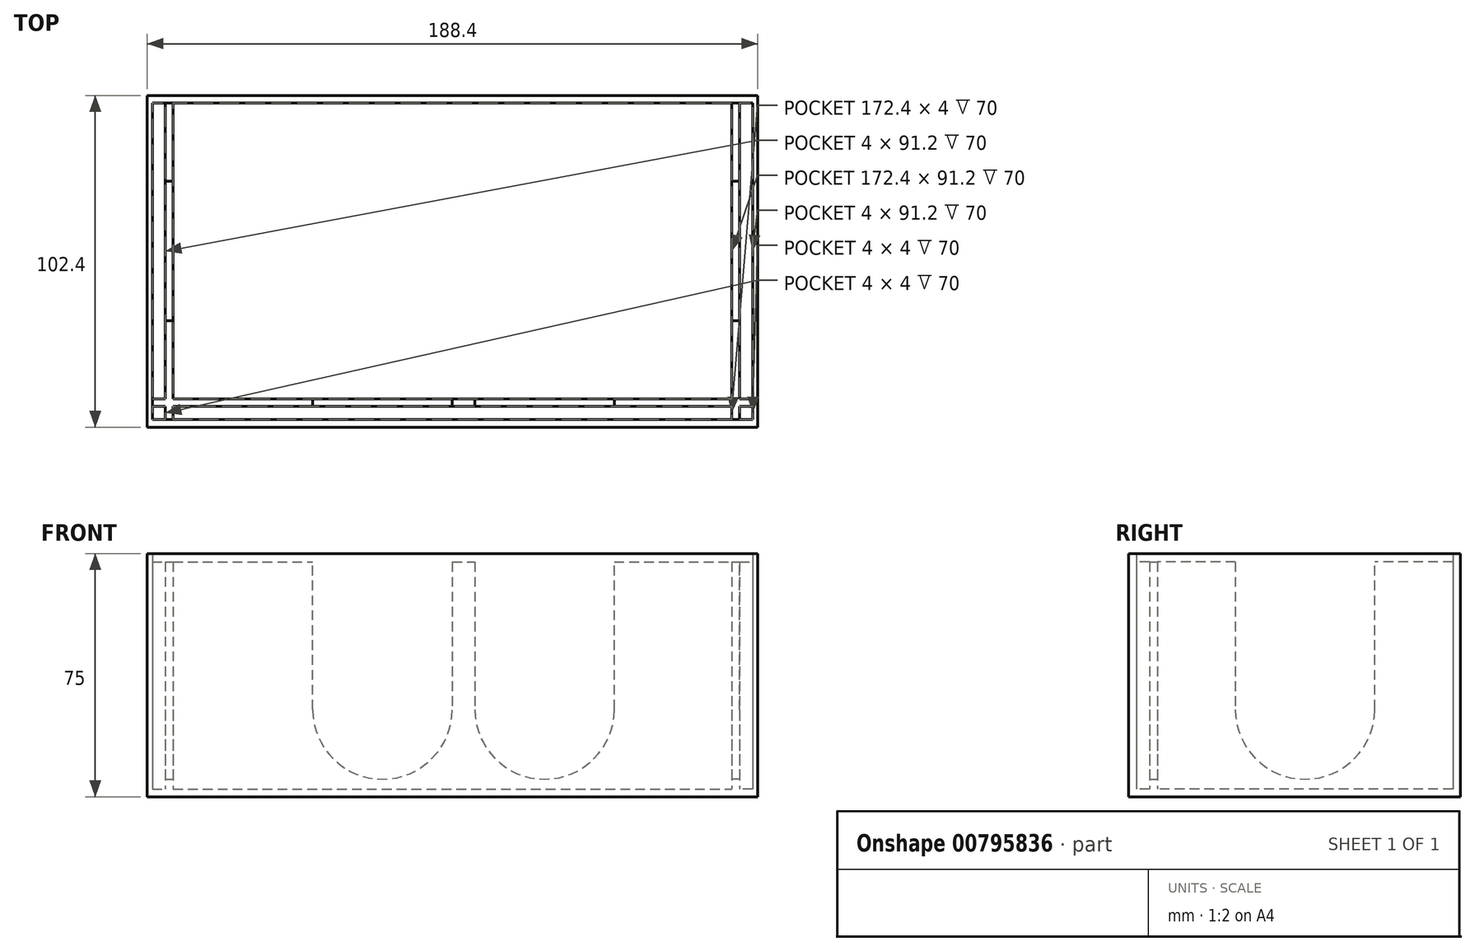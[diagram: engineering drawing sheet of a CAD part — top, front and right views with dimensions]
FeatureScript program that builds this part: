
annotation { "Feature Type Name" : "Feature", "Feature Type Description" : "" }
export const myFeature = defineFeature(function(context is Context, id is Id, definition is map)
    precondition{}
    {
        {
            var Q0;
            Q0=qCreatedBy(makeId("Top.planeOp"),FACE);
            var sketch = newSketch(context, id + "F0", { "sketchPlane" : qUnion([Q0]) });
            skLineSegment(sketch, "E0", {"start": v(-98.41, -24.68) * mm, "end": v(91.59, -24.68) * mm});
            skLineSegment(sketch, "E1", {"start": v(91.59, -24.68) * mm, "end": v(91.59, 77.72) * mm});
            skLineSegment(sketch, "E2", {"start": v(91.59, 77.72) * mm, "end": v(-98.41, 77.72) * mm});
            skLineSegment(sketch, "E3", {"start": v(-98.41, 77.72) * mm, "end": v(-98.41, -24.68) * mm});
            skSolve(sketch);
        }
        {
            var Q0;
            Q0 = qSketchRegion(id + "F0", true);
            extrude(context, id + "F1", {"entities" : qUnion([Q0]), "depth" : 75 * mm, "offsetDistance" : 25 * mm});
        }
        {
            var Q0;
            Q0=makeQuery(id+"F1.opExtrude","CAP_FACE",FACE,{"disambiguationData":[OSD([sQuery(id+"F0.wireOp",EDGE,"E0"),sQuery(id+"F0.wireOp",EDGE,"E1"),sQuery(id+"F0.wireOp",EDGE,"E2"),sQuery(id+"F0.wireOp",EDGE,"E3")])],"isStart":false});
            shell(context, id + "F2", {"entities" : qUnion([Q0]), "thickness" : 2.4 * mm});
        }
        {
            var Q0;
            Q0=makeQuery(id+"F2.opShell","OFFSET_FACE",FACE,{"disambiguationData":[OSD([sQuery(id+"F0.wireOp",EDGE,"E0"),sQuery(id+"F0.wireOp",EDGE,"E1"),sQuery(id+"F0.wireOp",EDGE,"E2"),sQuery(id+"F0.wireOp",EDGE,"E3")])]});
            var sketch = newSketch(context, id + "F3", { "sketchPlane" : qUnion([Q0]) });
            skLineSegment(sketch, "E4", {"start": v(-96.01, 75.32) * mm, "end": v(-92.01, 75.32) * mm, "construction": true});
            skLineSegment(sketch, "E5", {"start": v(-92.01, 75.32) * mm, "end": v(-89.61, 75.32) * mm});
            skLineSegment(sketch, "E6", {"start": v(-96.01, -22.28) * mm, "end": v(-96.01, -18.28) * mm, "construction": true});
            skLineSegment(sketch, "E7", {"start": v(-96.01, -18.28) * mm, "end": v(-96.01, -15.88) * mm});
            skLineSegment(sketch, "E8", {"start": v(89.19, 75.32) * mm, "end": v(85.19, 75.32) * mm, "construction": true});
            skLineSegment(sketch, "E9", {"start": v(85.19, 75.32) * mm, "end": v(82.79, 75.32) * mm});
            skLineSegment(sketch, "E10", {"start": v(-92.01, 75.32) * mm, "end": v(-92.01, -15.88) * mm});
            skLineSegment(sketch, "E11", {"start": v(-89.61, 75.32) * mm, "end": v(-89.61, -15.88) * mm});
            skLineSegment(sketch, "E12", {"start": v(-96.01, -18.28) * mm, "end": v(-92.01, -18.28) * mm});
            skLineSegment(sketch, "E13", {"start": v(-96.01, -15.88) * mm, "end": v(-92.01, -15.88) * mm});
            skLineSegment(sketch, "E14", {"start": v(85.19, 75.32) * mm, "end": v(85.19, -15.88) * mm});
            skLineSegment(sketch, "E15", {"start": v(82.79, 75.32) * mm, "end": v(82.79, -15.88) * mm});
            skLineSegment(sketch, "E16.trimOffspring", {"start": v(85.19, -15.88) * mm, "end": v(89.19, -15.88) * mm});
            skLineSegment(sketch, "E17.trimOffspring", {"start": v(82.79, -18.28) * mm, "end": v(82.79, -22.28) * mm});
            skLineSegment(sketch, "E18.trimOffspring", {"start": v(85.19, -18.28) * mm, "end": v(85.19, -22.28) * mm});
            skLineSegment(sketch, "E19.trimOffspring", {"start": v(85.19, -18.28) * mm, "end": v(89.19, -18.28) * mm});
            skLineSegment(sketch, "E20.trimOffspring", {"start": v(-89.61, -18.28) * mm, "end": v(82.79, -18.28) * mm});
            skLineSegment(sketch, "E21.trimOffspring", {"start": v(-89.61, -15.88) * mm, "end": v(82.79, -15.88) * mm});
            skLineSegment(sketch, "E22.trimOffspring", {"start": v(-92.01, -18.28) * mm, "end": v(-92.01, -22.28) * mm});
            skLineSegment(sketch, "E23.trimOffspring", {"start": v(-89.61, -18.28) * mm, "end": v(-89.61, -22.28) * mm});
            skLineSegment(sketch, "E24", {"start": v(-92.01, -22.28) * mm, "end": v(-89.61, -22.28) * mm});
            skLineSegment(sketch, "E25", {"start": v(82.79, -22.28) * mm, "end": v(85.19, -22.28) * mm});
            skLineSegment(sketch, "E26", {"start": v(89.19, -15.88) * mm, "end": v(89.19, -18.28) * mm});
            skLineSegment(sketch, "E27", {"start": v(82.79, 75.32) * mm, "end": v(85.19, 75.32) * mm});
            skSolve(sketch);
        }
        {
            var Q0;
            Q0 = qSketchRegion(id + "F3", true);
            extrude(context, id + "F4", {"entities" : qUnion([Q0]), "operationType" : NewBodyOperationType.ADD, "depth" : 70 * mm, "offsetDistance" : 25 * mm});
        }
        {
            var Q0;
            Q0=makeQuery(id+"F4.opExtrude","SWEPT_FACE",FACE,{"disambiguationData":[OSD([sQuery(id+"F3.wireOp",EDGE,"E15")])]});
            var sketch = newSketch(context, id + "F5", { "sketchPlane" : qUnion([Q0]) });
            skLineSegment(sketch, "E28", {"start": v(-29.72, 72.4) * mm, "end": v(-29.72, 2.4) * mm, "construction": true});
            skArc(sketch, "E29", {"start": v(-51.22, 26.9) * mm, "mid": v(-29.72, 5.4) * mm, "end": v(-8.22, 26.9) * mm});
            skLineSegment(sketch, "E30", {"start": v(-29.72, 26.9) * mm, "end": v(-29.72, 5.4) * mm, "construction": true});
            skLineSegment(sketch, "E31", {"start": v(-29.72, 5.4) * mm, "end": v(-29.72, 2.4) * mm, "construction": true});
            skLineSegment(sketch, "E32", {"start": v(-8.22, 26.9) * mm, "end": v(-51.22, 26.9) * mm, "construction": true});
            skLineSegment(sketch, "E33", {"start": v(-51.22, 26.9) * mm, "end": v(-51.22, 72.4) * mm});
            skLineSegment(sketch, "E34", {"start": v(-51.22, 72.4) * mm, "end": v(-8.22, 72.4) * mm});
            skLineSegment(sketch, "E35", {"start": v(-8.22, 72.4) * mm, "end": v(-8.22, 26.9) * mm});
            skSolve(sketch);
        }
        {
            var Q0;
            Q0 = qSketchRegion(id + "F5", true);
            extrude(context, id + "F6", {"entities" : qUnion([Q0]), "operationType" : NewBodyOperationType.REMOVE, "oppositeDirection" : true, "depth" : 2.6 * mm, "offsetDistance" : 25 * mm});
        }
        {
            var Q0;
            Q0 = qSketchRegion(id + "F5", true);
            extrude(context, id + "F7", {"entities" : qUnion([Q0]), "operationType" : NewBodyOperationType.REMOVE, "depth" : 176.9 * mm, "offsetDistance" : 25 * mm});
        }
        {
            var Q0;
            Q0=makeQuery(id+"F4.opExtrude","SWEPT_FACE",FACE,{"disambiguationData":[OSD([sQuery(id+"F3.wireOp",EDGE,"E21.trimOffspring")])]});
            var sketch = newSketch(context, id + "F8", { "sketchPlane" : qUnion([Q0]) });
            skLineSegment(sketch, "E36", {"start": v(0, 2.4) * mm, "end": v(0, 75.04) * mm, "construction": true});
            skLineSegment(sketch, "E37", {"start": v(0, 75.04) * mm, "end": v(50, 75.04) * mm, "construction": true});
            skLineSegment(sketch, "E38", {"start": v(25, 72.4) * mm, "end": v(25, 2.4) * mm, "construction": true});
            skPoint(sketch, "E38.startSnap0", {"position": v(25, 75.04) * mm});
            skArc(sketch, "E39", {"start": v(3.5, 26.9) * mm, "mid": v(25, 5.4) * mm, "end": v(46.5, 26.9) * mm});
            skLineSegment(sketch, "E40", {"start": v(25, 5.4) * mm, "end": v(25, 2.4) * mm, "construction": true});
            skLineSegment(sketch, "E41", {"start": v(3.5, 26.9) * mm, "end": v(46.5, 26.9) * mm, "construction": true});
            skLineSegment(sketch, "E42", {"start": v(46.5, 26.9) * mm, "end": v(46.5, 72.4) * mm});
            skLineSegment(sketch, "E43", {"start": v(46.5, 72.4) * mm, "end": v(3.5, 72.4) * mm});
            skLineSegment(sketch, "E44", {"start": v(3.5, 72.4) * mm, "end": v(3.5, 26.9) * mm});
            skLineSegment(sketch, "E45.MirrorCS", {"start": v(-46.5, 26.9) * mm, "end": v(-46.5, 72.4) * mm});
            skLineSegment(sketch, "E46.MirrorCS", {"start": v(-46.5, 72.4) * mm, "end": v(-3.5, 72.4) * mm});
            skLineSegment(sketch, "E47.MirrorCS", {"start": v(-3.5, 72.4) * mm, "end": v(-3.5, 26.9) * mm});
            skArc(sketch, "E48.MirrorCS", {"start": v(-3.5, 26.9) * mm, "mid": v(-25, 5.4) * mm, "end": v(-46.5, 26.9) * mm});
            skSolve(sketch);
        }
        {
            var Q0;
            Q0 = qSketchRegion(id + "F8", true);
            extrude(context, id + "F9", {"entities" : qUnion([Q0]), "operationType" : NewBodyOperationType.REMOVE, "oppositeDirection" : true, "depth" : 2.6 * mm, "offsetDistance" : 25 * mm});
        }
        {
            var Q0;
            Q0=makeQuery(id+"F1.opExtrude","CAP_FACE",FACE,{"disambiguationData":[OSD([sQuery(id+"F0.wireOp",EDGE,"E0"),sQuery(id+"F0.wireOp",EDGE,"E1"),sQuery(id+"F0.wireOp",EDGE,"E2"),sQuery(id+"F0.wireOp",EDGE,"E3")])],"isStart":false});
            var Q1;
            Q1=makeQuery(id+"F1.opExtrude","CAP_FACE",FACE,{"disambiguationData":[OSD([sQuery(id+"F0.wireOp",EDGE,"E0"),sQuery(id+"F0.wireOp",EDGE,"E1"),sQuery(id+"F0.wireOp",EDGE,"E2"),sQuery(id+"F0.wireOp",EDGE,"E3")])],"isStart":false});
            var sketch = newSketch(context, id + "F10", { "sketchPlane" : qUnion([Q0, Q1]) });
            skLineSegment(sketch, "E49", {"start": v(-98.41, 77.72) * mm, "end": v(-97.61, 77.72) * mm});
            skLineSegment(sketch, "E50", {"start": v(-97.61, 77.72) * mm, "end": v(-97.61, -24.68) * mm});
            skLineSegment(sketch, "E51", {"start": v(-98.41, -24.68) * mm, "end": v(-97.61, -24.68) * mm});
            skLineSegment(sketch, "E52", {"start": v(-98.41, -24.68) * mm, "end": v(-98.41, 77.72) * mm});
            skLineSegment(sketch, "E53", {"start": v(90.79, 77.72) * mm, "end": v(91.59, 77.72) * mm});
            skLineSegment(sketch, "E54", {"start": v(91.59, 77.72) * mm, "end": v(91.59, -24.68) * mm});
            skLineSegment(sketch, "E55", {"start": v(90.79, 77.72) * mm, "end": v(90.79, -24.68) * mm});
            skLineSegment(sketch, "E56", {"start": v(90.79, -24.68) * mm, "end": v(91.59, -24.68) * mm});
            skSolve(sketch);
        }
        {
            var Q0;
            Q0 = qSketchRegion(id + "F10", true);
            extrude(context, id + "F11", {"entities" : qUnion([Q0]), "operationType" : NewBodyOperationType.REMOVE, "oppositeDirection" : true, "depth" : 75 * mm, "offsetDistance" : 25 * mm});
        }
    });
